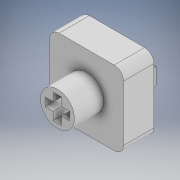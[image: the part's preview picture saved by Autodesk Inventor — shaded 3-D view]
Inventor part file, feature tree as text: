
AUTODESK INVENTOR PART (.ipt)
format: ipt  version: 2022 (Build 260153000, 153)  size: 260,608 bytes
history: native  units: in
note: dims shown in document units (in); Inventor stores cm internally (conversion verified against a paired STEP export)
features: sketch x4, extrude x3, plane x1, projected_geometry x1
ambient origin geometry x8: Origin, YZ Plane, XZ Plane, XY Plane, X Axis, Y Axis, Z Axis, Center Point
bodies: Body1 (feature_tree)
feature tree (9):
  sketch  "Sketch1"  dims[d3=0.2205in d4=0.1594in]
  plane  "Work Plane1"
  sketch  "Sketch2"  dims[d5=0.0531in d6=0.1594in]
  extrude  "Extrusion3"  Depth=0.1594in
  extrude  "Extrusion4"  Depth=0.1594in
  extrude  "Extrusion5"  Depth=0.5016in
  projected_geometry  "Projected Loop1"
  sketch  "Sketch3"  dims[d7=0.0531in d10=0.5016in]
  sketch  "Sketch4"  dims[d12=0.1969in d13=0.0in d14=0.2205in d15=0.1594in d16=0.0531in d17=0.1594in d18=0.0531in d19=0.189in d20=0.0in d21=0.0892in d22=0.2693in d23=0.0354in d24=0.0in]
